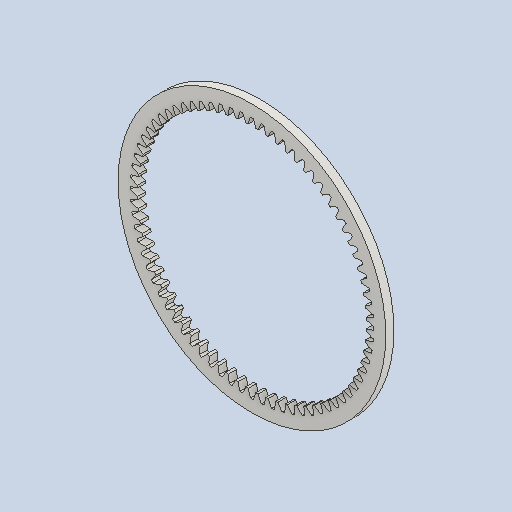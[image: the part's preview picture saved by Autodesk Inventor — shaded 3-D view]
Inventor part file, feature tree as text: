
AUTODESK INVENTOR PART (.ipt)
format: ipt  version: 2024 (Build 280153000, 153)  size: 404,480 bytes
history: native  units: mm (DEFAULTED — no unit token found)
features: plane x3, other x3, extrude x1, sketch x1
ambient origin geometry x8: Origin, YZ Plane, XZ Plane, XY Plane, X Axis, Y Axis, Z Axis, Center Point
bodies: Solid1 (feature_tree)
feature tree (8):
  extrude  "Extrusion1"  Depth=5.0mm TaperAngle=0.0deg
  plane  "Work Plane2"
  plane  "Work Plane8"
  plane  "Work Plane9"
  other  "Spur Gear"
  sketch  "Sketch1"  dims[d0=163.9mm d1=5.0mm d2=0.0mm d3=144.0mm d4=10.0mm d5=0.0mm d16=54.0mm d17=0.0mm d34=0.436332mm d39=0.0mm d45=0.0mm d47=54.0mm d50=0.0mm d51=0.0mm d52=54.0mm]
  other  "Srf1"
  other  "Pitch Diameter"
